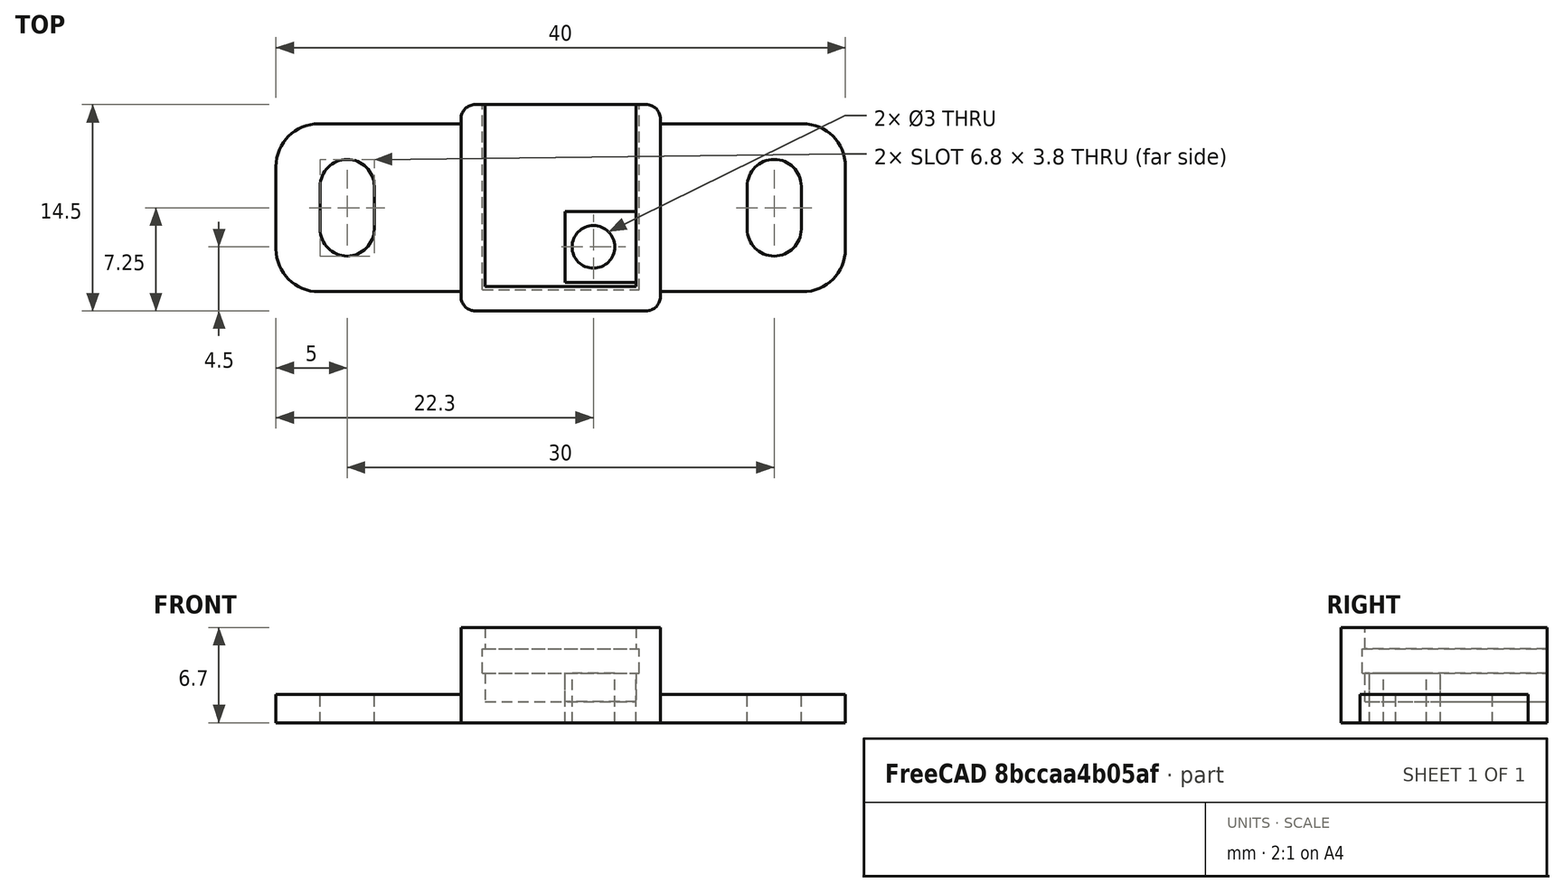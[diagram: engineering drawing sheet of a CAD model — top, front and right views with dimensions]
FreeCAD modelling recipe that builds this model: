
FCSTD DOCUMENT  (FreeCAD 0.19R23578 (Git))
Label: gy-21_si7021
License: FreeArt
LicenseURL: http://artlibre.org/licence/lal
objects: Part::Box×4, Part::MultiFuse×3, Part::Cut×3, Spreadsheet::Sheet×1, Part::Fillet×1, Part::Cylinder×1, Part::Feature×1, App::Part×1
note: 13 computed .brp shape members not serialized (recipe doc carries the construction recipe); baked Part::Feature solids carry a one-line shape summary decoded from their .brp

FEATURE [Spreadsheet::Sheet] Spreadsheet  label="p"
  cells = A1=pcb_x; B1(pcb_x)==11mm; A2=pcb_y; B2(pcb_y)==13mm; A3=pcb_z; B3(pcb_z)==1.7mm; A4=pcb_under; B4(pcb_under)==2mm; A5=side_wall; B5(side_wall)==1.5mm; A6=pcb_side_lane; B6(pcb_side_lane)==0.2mm; A7=bottom_wall; B7(bottom_wall)==1.5mm; A8=pcb_above; B8(pcb_above)==1.5mm; A9=hole_dist_x; B9(hole_dist_x)==23.5mm; A10=hole_r; B10(hole_r)==1.5mm; A11=hole_off_x; B11(hole_off_x)==7.8mm; A12=hole_off_y; B12(hole_off_y)==3mm; A13=hole_stand_size; B13(hole_stand_size)==5mm
FEATURE [Part::Box] Box  label="external cube"
  AttacherType = Attacher::AttachEngine3D
  Height = 6.7
  Length = 14
  Width = 14.5
  expr: Height = <<p>>.bottom_wall + <<p>>.pcb_under + <<p>>.pcb_z + <<p>>.pcb_above
  expr: Width = <<p>>.pcb_y + <<p>>.side_wall
  expr: Length = <<p>>.pcb_x + 2 * <<p>>.side_wall
FEATURE [Part::Box] Box006  label="internal cube"
  AttacherType = Attacher::AttachEngine3D
  Height = 5.2
  Length = 10.6
  Placement = pos=(1.7,1.7,1.5) rot=(0,0,1;0rad)
  Width = 14.1
  expr: .Placement.Base.y = <<p>>.side_wall + <<p>>.pcb_side_lane
  expr: .Placement.Base.x = <<p>>.side_wall + <<p>>.pcb_side_lane
  expr: .Placement.Base.z = <<p>>.bottom_wall
  expr: Height = <<p>>.pcb_under + <<p>>.pcb_z + <<p>>.pcb_above
  expr: Width = <<p>>.pcb_y - 2 * <<p>>.pcb_side_lane + <<p>>.side_wall
  expr: Length = <<p>>.pcb_x - 2 * <<p>>.pcb_side_lane
FEATURE [Part::Box] Box007  label="pcb extract cube"
  AttacherType = Attacher::AttachEngine3D
  Height = 1.7
  Length = 11
  Placement = pos=(1.5,1.5,3.5) rot=(0,0,1;0rad)
  Width = 13
  expr: .Placement.Base.y = <<p>>.side_wall
  expr: .Placement.Base.x = <<p>>.side_wall
  expr: Length = <<p>>.pcb_x
  expr: Width = <<p>>.pcb_y
  expr: .Placement.Base.z = <<p>>.bottom_wall + <<p>>.pcb_under
  expr: Height = <<p>>.pcb_z
FEATURE [Part::MultiFuse] Fusion  label="extract fusion"
  Shapes = -> [Box006,Box007]
FEATURE [Part::Fillet] Fillet  label="external fillet"
  Base = -> Box
  Edges = 4 edges r=1: [Edge1,Edge3,Edge5,Edge7]
FEATURE [Part::Cylinder] Cylinder  label="hole"
  Angle = 360
  AttacherType = Attacher::AttachEngine3D
  Height = 10
  Placement = pos=(9.3,4.5,0) rot=(0,0,1;0rad)
  Radius = 1.5
  expr: .Placement.Base.y = <<p>>.hole_off_y + <<p>>.side_wall
  expr: .Placement.Base.x = <<p>>.side_wall + <<p>>.hole_off_x
  expr: Radius = <<p>>.hole_r
FEATURE [Part::Box] Box008  label="stand"
  AttacherType = Attacher::AttachEngine3D
  Height = 3.5
  Length = 5
  Placement = pos=(7.3,2,0) rot=(0,0,1;0rad)
  Width = 5
  expr: Height = <<p>>.pcb_under + <<p>>.bottom_wall
  expr: Length = <<p>>.hole_stand_size
  expr: Width = <<p>>.hole_stand_size
  expr: .Placement.Base.x = <<p>>.side_wall + <<p>>.hole_off_x - <<p>>.hole_stand_size / 2 + 0.5mm
  expr: .Placement.Base.y = <<p>>.hole_off_y + <<p>>.side_wall - <<p>>.hole_stand_size / 2
FEATURE [Part::Cut] Cut003002  label="stand hole cut"
  Base = -> Box008
  Tool = -> Cylinder
FEATURE [Part::Feature] Cut003001  label="attach plane x dir001"
  Placement = pos=(-13,1.35,0) rot=(0,0,1;0rad)
  shape: bbox 40 x 11.8 x 2 mm, 18 faces (baked)
FEATURE [Part::MultiFuse] Fusion001  label="body fusion"
  Shapes = -> [Fillet,Cut003001]
FEATURE [Part::Cut] Cut  label="body cut003"
  Base = -> Fusion001
  Tool = -> Fusion
FEATURE [Part::MultiFuse] Fusion002  label="body fusion003"
  Shapes = -> [Cut,Box008]
FEATURE [Part::Cut] Cut003003  label="body cut"
  Base = -> Fusion002
  Tool = -> Cylinder
FEATURE [App::Part] Part  label="box part"
  Group = -> [Box,Fillet,Fusion001,Fusion,Box007,Box006,Cut,Cylinder,Box008,Cut003002,Fusion002,Cut003003]
  Origin = -> Origin
